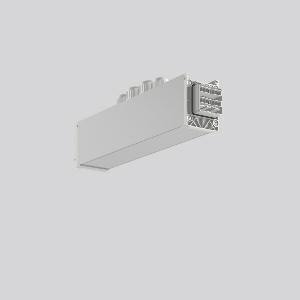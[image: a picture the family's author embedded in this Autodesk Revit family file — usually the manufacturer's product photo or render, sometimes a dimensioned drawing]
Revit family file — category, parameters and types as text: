
# Revit family: linedo_mitteleinspeisung_14pol_s_s_982698_000_2_e352
name_source: partatom
category: Lighting Fixtures
units: mm (PartAtom-declared; Revit-internal decimal feet)

## family parameters
Cut with Voids When Loaded = No
Host = Face
Light Source = No
Part Type = Normal
Room Calculation Point = No
Round Connector Dimension = Use Diameter
Shared = No

## types (1)
- LINEDO_Mitteleinspeisung_14pol_S_S
    Apparent Load = 0 VA
    Default Elevation = 1800 mm
    Description = Series: LINEDO
Middle power feed, 14-pole, connection plug / plug. Housing: extruded aluminium profile, anodised. Cover made of plastic, surface like housing. LINEDO plug system, plastic, light grey. 4 cable glands (2 x M20 and 2 x M25). Cable glands on top. Easy connection for rigid or flexible wires.
Colour: anodised aluminium
Length: 349 mm
Width: 58 mm
Height: 76 mm
Weight: 850 g
    Height = 76 mm
    Lamp = 0 x
    Length = 349 mm
    Luminous efficacy = 0 lm/W
    Manufacturer = RZB
    ModVariant = No
    Model = 982698.000.2
    Mounting Place = Ceiling
    Mounting Type = Pendant, Surface mounted
    Number of Poles = 1
    OnlyDefault = Yes
    Power Factor = 1
    Product Name = LINEDO_Mitteleinspeisung_14pol_S_S
    Product group = Surface mounted continuous line luminaire system
    ProductGroupID = 310
    Protection Class = Protection class I
    Protection Degree = IP 54
    RLX_Detail_Level = 1
    RLX_Emergency_Light_Flux = 0 lm
    RLX_Emergency_Type = 0
    RLX_Emergency_Type_DB = No
    RlxData = <blob elided: 21897 chars, md5=f6d836f3>
    Standby Power = 0 W
    System Light Flux = 0 lm
    System Power = 0 W
    Type Comments = Product without accessories
    Type Image = 982698.000.2.jpg
    URL = http://relux.com
    VarID = ---
    Voltage = 0 V
    Weight = 0.00 kg
    Width = 58 mm

## geometry (parser evidence)
native form markers: Blend x4, Sweep x12
no freeform markers — native parametric forms only
